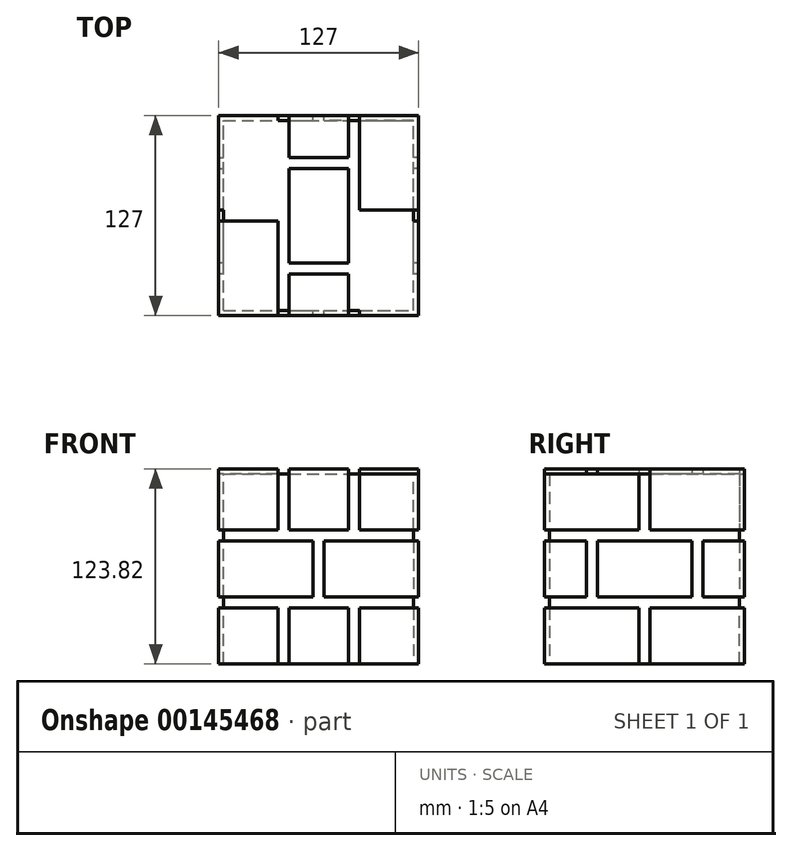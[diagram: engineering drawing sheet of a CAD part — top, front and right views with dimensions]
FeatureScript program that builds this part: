
annotation { "Feature Type Name" : "Feature", "Feature Type Description" : "" }
export const myFeature = defineFeature(function(context is Context, id is Id, definition is map)
    precondition{}
    {
        {
            var Q0;
            Q0=qCreatedBy(makeId("Front.planeOp"),FACE);
            var sketch = newSketch(context, id + "F0", { "sketchPlane" : qUnion([Q0])});
            skLineSegment(sketch, "E0.bottom", {"start": v(60.33, 60.33) * mm, "end": v(-60.33, 60.33) * mm});
            skLineSegment(sketch, "E0.top", {"start": v(60.32, -60.33) * mm, "end": v(-60.33, -60.33) * mm});
            skLineSegment(sketch, "E0.left", {"start": v(60.33, 60.33) * mm, "end": v(60.32, -60.33) * mm});
            skLineSegment(sketch, "E0.right", {"start": v(-60.33, 60.33) * mm, "end": v(-60.33, -60.33) * mm});
            skPoint(sketch, "E0.middle", {"position": v(0, 0) * mm});
            skSolve(sketch);
        }
        {
            var Q0;
            Q0 = qSketchRegion(id + "F0", true);
            extrude(context, id + "F1", {"entities" : qUnion([Q0]), "depth" : 60.32 * mm, "hasSecondDirection" : true, "secondDirectionOppositeDirection" : true, "secondDirectionDepth" : 60.32 * mm});
        }
        {
            var Q0;
            Q0=makeQuery(id+"F1.opExtrude","CAP_FACE",FACE,{"disambiguationData":[OSD([sQuery(id+"F0.wireOp",EDGE,"E0.bottom"),sQuery(id+"F0.wireOp",EDGE,"E0.top"),sQuery(id+"F0.wireOp",EDGE,"E0.left"),sQuery(id+"F0.wireOp",EDGE,"E0.right")])],"isStart":false});
            var sketch = newSketch(context, id + "F2", { "sketchPlane" : qUnion([Q0])});
            skLineSegment(sketch, "E1", {"start": v(-63.5, -60.33) * mm, "end": v(-63.5, -24.77) * mm});
            skLineSegment(sketch, "E2", {"start": v(-63.5, -24.77) * mm, "end": v(-25.9, -24.77) * mm});
            skLineSegment(sketch, "E3", {"start": v(-25.9, -24.77) * mm, "end": v(-25.9, -60.33) * mm});
            skLineSegment(sketch, "E4", {"start": v(-25.9, -60.33) * mm, "end": v(-63.5, -60.33) * mm});
            skLineSegment(sketch, "E5", {"start": v(-63.5, 17.78) * mm, "end": v(-3.5, 17.78) * mm});
            skLineSegment(sketch, "E6", {"start": v(-3.5, 17.78) * mm, "end": v(-3.5, -17.78) * mm});
            skLineSegment(sketch, "E7", {"start": v(-3.5, -17.78) * mm, "end": v(-63.5, -17.78) * mm});
            skLineSegment(sketch, "E8", {"start": v(-63.5, -17.78) * mm, "end": v(-63.5, 17.78) * mm});
            skLineSegment(sketch, "E9", {"start": v(3.5, 17.78) * mm, "end": v(3.5, -17.78) * mm});
            skLineSegment(sketch, "E10", {"start": v(3.5, -17.78) * mm, "end": v(63.5, -17.78) * mm});
            skLineSegment(sketch, "E11", {"start": v(63.5, -17.78) * mm, "end": v(63.5, 17.78) * mm});
            skLineSegment(sketch, "E12", {"start": v(63.5, 17.78) * mm, "end": v(3.5, 17.78) * mm});
            skLineSegment(sketch, "E13", {"start": v(-18.92, -60.33) * mm, "end": v(-18.92, -24.77) * mm});
            skLineSegment(sketch, "E14", {"start": v(-18.92, -24.77) * mm, "end": v(18.92, -24.77) * mm});
            skLineSegment(sketch, "E15", {"start": v(18.92, -24.77) * mm, "end": v(18.92, -60.33) * mm});
            skLineSegment(sketch, "E16", {"start": v(18.92, -60.33) * mm, "end": v(-18.92, -60.33) * mm});
            skLineSegment(sketch, "E17", {"start": v(25.9, -60.33) * mm, "end": v(25.9, -24.77) * mm});
            skLineSegment(sketch, "E18", {"start": v(25.9, -24.77) * mm, "end": v(63.5, -24.77) * mm});
            skLineSegment(sketch, "E19", {"start": v(63.5, -24.77) * mm, "end": v(63.5, -60.33) * mm});
            skLineSegment(sketch, "E20", {"start": v(63.5, -60.33) * mm, "end": v(25.9, -60.33) * mm});
            skLineSegment(sketch, "E21.MirrorCS", {"start": v(-63.5, 24.77) * mm, "end": v(-25.9, 24.77) * mm});
            skLineSegment(sketch, "E22.MirrorCS", {"start": v(-25.9, 24.77) * mm, "end": v(-25.9, 60.33) * mm});
            skLineSegment(sketch, "E23.MirrorCS", {"start": v(-25.9, 60.33) * mm, "end": v(-63.5, 60.33) * mm});
            skLineSegment(sketch, "E24.MirrorCS", {"start": v(-63.5, 60.33) * mm, "end": v(-63.5, 24.77) * mm});
            skLineSegment(sketch, "E25.MirrorCS", {"start": v(-18.92, 24.77) * mm, "end": v(18.92, 24.77) * mm});
            skLineSegment(sketch, "E26.MirrorCS", {"start": v(-18.92, 60.33) * mm, "end": v(-18.92, 24.77) * mm});
            skLineSegment(sketch, "E27.MirrorCS", {"start": v(18.92, 60.33) * mm, "end": v(-18.92, 60.33) * mm});
            skLineSegment(sketch, "E28.MirrorCS", {"start": v(18.92, 24.77) * mm, "end": v(18.92, 60.33) * mm});
            skLineSegment(sketch, "E29.MirrorCS", {"start": v(25.9, 24.77) * mm, "end": v(63.5, 24.77) * mm});
            skLineSegment(sketch, "E30.MirrorCS", {"start": v(25.9, 60.33) * mm, "end": v(25.9, 24.77) * mm});
            skLineSegment(sketch, "E31.MirrorCS", {"start": v(63.5, 60.33) * mm, "end": v(25.9, 60.33) * mm});
            skLineSegment(sketch, "E32.MirrorCS", {"start": v(63.5, 24.77) * mm, "end": v(63.5, 60.33) * mm});
            skLineSegment(sketch, "E33", {"start": v(-60.33, 24.76) * mm, "end": v(-60.33, 17.78) * mm});
            skSolve(sketch);
        }
        {
            var Q0;
            {var subQ0=sQuery(id+"F2.wireOp",EDGE,"E22.MirrorCS");Q0=makeQuery(id+"F2.imprint","IMPRINT",FACE,{"disambiguationData":[TD([[makeQuery(id+"F2.imprint","IMPRINT",EDGE,{"derivedFrom":subQ0}),1.0]])]});}
            var Q1;
            Q1=makeQuery(id+"F2.imprint","IMPRINT",FACE,{"disambiguationData":[TD([[makeQuery(id+"F2.imprint","IMPRINT",EDGE,{"derivedFrom":sQuery(id+"F2.wireOp",EDGE,"E26.MirrorCS")}),1.0]])]});
            var Q2;
            {var subQ0=sQuery(id+"F2.wireOp",EDGE,"E30.MirrorCS");Q2=makeQuery(id+"F2.imprint","IMPRINT",FACE,{"disambiguationData":[TD([[makeQuery(id+"F2.imprint","IMPRINT",EDGE,{"derivedFrom":subQ0}),1.0]])]});}
            var Q3;
            {var subQ0=sQuery(id+"F2.wireOp",EDGE,"E9");Q3=makeQuery(id+"F2.imprint","IMPRINT",FACE,{"disambiguationData":[TD([[makeQuery(id+"F2.imprint","IMPRINT",EDGE,{"derivedFrom":subQ0}),1.0]])]});}
            var Q4;
            {var subQ0=sQuery(id+"F2.wireOp",EDGE,"E6");Q4=makeQuery(id+"F2.imprint","IMPRINT",FACE,{"disambiguationData":[TD([[makeQuery(id+"F2.imprint","IMPRINT",EDGE,{"derivedFrom":subQ0}),-1.0]])]});}
            var Q5;
            {var subQ0=sQuery(id+"F2.wireOp",EDGE,"E3");Q5=makeQuery(id+"F2.imprint","IMPRINT",FACE,{"disambiguationData":[TD([[makeQuery(id+"F2.imprint","IMPRINT",EDGE,{"derivedFrom":subQ0}),-1.0]])]});}
            var Q6;
            Q6=makeQuery(id+"F2.imprint","IMPRINT",FACE,{"disambiguationData":[TD([[makeQuery(id+"F2.imprint","IMPRINT",EDGE,{"derivedFrom":sQuery(id+"F2.wireOp",EDGE,"E13")}),-1.0]])]});
            var Q7;
            {var subQ0=sQuery(id+"F2.wireOp",EDGE,"E17");Q7=makeQuery(id+"F2.imprint","IMPRINT",FACE,{"disambiguationData":[TD([[makeQuery(id+"F2.imprint","IMPRINT",EDGE,{"derivedFrom":subQ0}),-1.0]])]});}
            extrude(context, id + "F3", {"entities" : qUnion([Q0, Q1, Q2, Q3, Q4, Q5, Q6, Q7]), "operationType" : NewBodyOperationType.ADD, "depth" : 3.17 * mm});
        }
        {
            var Q0;
            {var subQ0=sQuery(id+"F0.wireOp",EDGE,"E0.left");var subQ1=makeQuery(id+"F1.opExtrude","CAP_EDGE",EDGE,{"disambiguationData":[OSD([subQ0])],"isStart":false});Q0=makeQuery(id+"F3.boolean.opBoolean","MERGE",FACE,{"derivedFrom":[makeQuery(id+"F1.opExtrude","SWEPT_FACE",FACE,{"disambiguationData":[OSD([subQ0])]}),makeQuery(id+"F3.opExtrude","SWEPT_FACE",FACE,{"disambiguationData":[OSD([subQ0]),TDD([makeQuery(id+"F2.imprint","IMPRINT",EDGE,{"disambiguationData":[TD([[makeQuery(id+"F2.imprint","INTERSECT",VERTEX,{"derivedFrom":[subQ1,sQuery(id+"F2.wireOp",EDGE,"E31.MirrorCS")]}),-1.0]])],"derivedFrom":subQ1})])]}),makeQuery(id+"F3.opExtrude","SWEPT_FACE",FACE,{"disambiguationData":[OSD([subQ0]),TDD([makeQuery(id+"F2.imprint","IMPRINT",EDGE,{"disambiguationData":[TD([[makeQuery(id+"F2.imprint","INTERSECT",VERTEX,{"derivedFrom":[subQ1,sQuery(id+"F2.wireOp",EDGE,"E20")]}),1.0]])],"derivedFrom":subQ1})])]}),makeQuery(id+"F3.opExtrude","SWEPT_FACE",FACE,{"disambiguationData":[OSD([subQ0]),TDD([makeQuery(id+"F2.imprint","IMPRINT",EDGE,{"disambiguationData":[TD([[makeQuery(id+"F2.imprint","INTERSECT",VERTEX,{"derivedFrom":[subQ1,sQuery(id+"F2.wireOp",EDGE,"E10")]}),1.0]])],"derivedFrom":subQ1})])]})]});}
            var sketch = newSketch(context, id + "F4", { "sketchPlane" : qUnion([Q0])});
            skLineSegment(sketch, "E34.bottom", {"start": v(-63.5, 17.78) * mm, "end": v(-37, 17.78) * mm});
            skLineSegment(sketch, "E34.top", {"start": v(-63.5, -17.78) * mm, "end": v(-37, -17.78) * mm});
            skLineSegment(sketch, "E34.left", {"start": v(-63.5, 17.78) * mm, "end": v(-63.5, -17.78) * mm});
            skLineSegment(sketch, "E34.right", {"start": v(-37, 17.78) * mm, "end": v(-37, -17.78) * mm});
            skLineSegment(sketch, "E35.bottom", {"start": v(-30.01, 17.78) * mm, "end": v(30, 17.78) * mm});
            skLineSegment(sketch, "E35.top", {"start": v(-30.01, -17.78) * mm, "end": v(30, -17.78) * mm});
            skLineSegment(sketch, "E35.left", {"start": v(-30.01, 17.78) * mm, "end": v(-30.01, -17.78) * mm});
            skLineSegment(sketch, "E35.right", {"start": v(30, 17.78) * mm, "end": v(30, -17.78) * mm});
            skLineSegment(sketch, "E36.bottom", {"start": v(36.98, 17.78) * mm, "end": v(63.5, 17.78) * mm});
            skLineSegment(sketch, "E36.top", {"start": v(36.98, -17.78) * mm, "end": v(63.5, -17.78) * mm});
            skLineSegment(sketch, "E36.left", {"start": v(36.98, 17.78) * mm, "end": v(36.98, -17.78) * mm});
            skLineSegment(sketch, "E36.right", {"start": v(63.5, 17.78) * mm, "end": v(63.5, -17.78) * mm});
            skLineSegment(sketch, "E37.bottom", {"start": v(-63.5, -24.76) * mm, "end": v(-3.5, -24.76) * mm});
            skLineSegment(sketch, "E37.top", {"start": v(-63.5, -60.32) * mm, "end": v(-3.5, -60.32) * mm});
            skLineSegment(sketch, "E37.left", {"start": v(-63.5, -24.76) * mm, "end": v(-63.5, -60.32) * mm});
            skLineSegment(sketch, "E37.right", {"start": v(-3.5, -24.76) * mm, "end": v(-3.5, -60.32) * mm});
            skLineSegment(sketch, "E38.bottom", {"start": v(3.5, -24.77) * mm, "end": v(63.5, -24.77) * mm});
            skLineSegment(sketch, "E38.top", {"start": v(3.5, -60.32) * mm, "end": v(63.5, -60.32) * mm});
            skLineSegment(sketch, "E38.left", {"start": v(3.5, -24.77) * mm, "end": v(3.5, -60.32) * mm});
            skLineSegment(sketch, "E38.right", {"start": v(63.5, -24.77) * mm, "end": v(63.5, -60.32) * mm});
            skLineSegment(sketch, "E39.MirrorCS", {"start": v(3.5, 24.77) * mm, "end": v(3.5, 60.33) * mm});
            skLineSegment(sketch, "E40.MirrorCS", {"start": v(3.5, 24.77) * mm, "end": v(63.5, 24.77) * mm});
            skLineSegment(sketch, "E41.MirrorCS", {"start": v(63.5, 24.77) * mm, "end": v(63.5, 60.33) * mm});
            skLineSegment(sketch, "E42.MirrorCS", {"start": v(3.5, 60.33) * mm, "end": v(63.5, 60.33) * mm});
            skLineSegment(sketch, "E43.MirrorCS", {"start": v(-3.5, 24.77) * mm, "end": v(-3.5, 60.33) * mm});
            skLineSegment(sketch, "E44.MirrorCS", {"start": v(-63.5, 24.77) * mm, "end": v(-3.5, 24.77) * mm});
            skLineSegment(sketch, "E45.MirrorCS", {"start": v(-63.5, 24.77) * mm, "end": v(-63.5, 60.33) * mm});
            skLineSegment(sketch, "E46.MirrorCS", {"start": v(-63.5, 60.33) * mm, "end": v(-3.5, 60.33) * mm});
            skSolve(sketch);
        }
        {
            var Q0;
            {var subQ1=sQuery(id+"F4.wireOp",EDGE,"E43.MirrorCS");Q0=makeQuery(id+"F4.imprint","IMPRINT",FACE,{"disambiguationData":[TD([[makeQuery(id+"F4.imprint","IMPRINT",EDGE,{"derivedFrom":subQ1}),1.0]])]});}
            var Q1;
            {var subQ0=sQuery(id+"F4.wireOp",EDGE,"E39.MirrorCS");Q1=makeQuery(id+"F4.imprint","IMPRINT",FACE,{"disambiguationData":[TD([[makeQuery(id+"F4.imprint","IMPRINT",EDGE,{"derivedFrom":subQ0}),-1.0]])]});}
            var Q2;
            {var subQ0=sQuery(id+"F4.wireOp",EDGE,"E36.left");Q2=makeQuery(id+"F4.imprint","IMPRINT",FACE,{"disambiguationData":[TD([[makeQuery(id+"F4.imprint","IMPRINT",EDGE,{"derivedFrom":subQ0}),1.0]])]});}
            var Q3;
            Q3=makeQuery(id+"F4.imprint","IMPRINT",FACE,{"disambiguationData":[TD([[makeQuery(id+"F4.imprint","IMPRINT",EDGE,{"derivedFrom":sQuery(id+"F4.wireOp",EDGE,"E35.bottom")}),-1.0]])]});
            var Q4;
            {var subQ0=sQuery(id+"F4.wireOp",EDGE,"E34.left");Q4=makeQuery(id+"F4.imprint","IMPRINT",FACE,{"disambiguationData":[TD([[makeQuery(id+"F4.imprint","IMPRINT",EDGE,{"derivedFrom":subQ0}),1.0]])]});}
            var Q5;
            Q5=makeQuery(id+"F4.imprint","IMPRINT",FACE,{"disambiguationData":[TD([[makeQuery(id+"F4.imprint","IMPRINT",EDGE,{"derivedFrom":sQuery(id+"F4.wireOp",EDGE,"E37.top")}),1.0]])]});
            var Q6;
            {var subQ0=sQuery(id+"F4.wireOp",EDGE,"E38.left");Q6=makeQuery(id+"F4.imprint","IMPRINT",FACE,{"disambiguationData":[TD([[makeQuery(id+"F4.imprint","IMPRINT",EDGE,{"derivedFrom":subQ0}),1.0]])]});}
            extrude(context, id + "F5", {"entities" : qUnion([Q0, Q1, Q2, Q3, Q4, Q5, Q6]), "operationType" : NewBodyOperationType.ADD, "depth" : 3.17 * mm});
        }
        {
            var Q0;
            {var subQ0=sQuery(id+"F0.wireOp",EDGE,"E0.left");var subQ1=makeQuery(id+"F1.opExtrude","CAP_EDGE",EDGE,{"disambiguationData":[OSD([subQ0])],"isStart":true});Q0=makeQuery(id+"F5.boolean.opBoolean","MERGE",FACE,{"derivedFrom":[makeQuery(id+"F1.opExtrude","CAP_FACE",FACE,{"disambiguationData":[OSD([sQuery(id+"F0.wireOp",EDGE,"E0.bottom"),sQuery(id+"F0.wireOp",EDGE,"E0.top"),subQ0,sQuery(id+"F0.wireOp",EDGE,"E0.right")])],"isStart":true}),makeQuery(id+"F5.opExtrude","SWEPT_FACE",FACE,{"disambiguationData":[OSD([subQ0]),TDD([makeQuery(id+"F4.imprint","IMPRINT",EDGE,{"disambiguationData":[TD([[makeQuery(id+"F4.imprint","INTERSECT",VERTEX,{"derivedFrom":[subQ1,sQuery(id+"F4.wireOp",EDGE,"E42.MirrorCS")]}),-1.0]])],"derivedFrom":subQ1})])]}),makeQuery(id+"F5.opExtrude","SWEPT_FACE",FACE,{"disambiguationData":[OSD([subQ0]),TDD([makeQuery(id+"F4.imprint","IMPRINT",EDGE,{"disambiguationData":[TD([[makeQuery(id+"F4.imprint","INTERSECT",VERTEX,{"derivedFrom":[subQ1,sQuery(id+"F4.wireOp",EDGE,"E38.top")]}),1.0]])],"derivedFrom":subQ1})])]}),makeQuery(id+"F5.opExtrude","SWEPT_FACE",FACE,{"disambiguationData":[OSD([subQ0]),TDD([makeQuery(id+"F4.imprint","IMPRINT",EDGE,{"disambiguationData":[TD([[makeQuery(id+"F4.imprint","INTERSECT",VERTEX,{"derivedFrom":[subQ1,sQuery(id+"F4.wireOp",EDGE,"E36.bottom")]}),-1.0]])],"derivedFrom":subQ1})])]})]});}
            var sketch = newSketch(context, id + "F6", { "sketchPlane" : qUnion([Q0])});
            skSolve(sketch);
        }
        {
            var Q0;
            Q0 = qSketchRegion(id + "F6", true);
            var Q1;
            Q1=makeQuery(id+"F3.opExtrude","CAP_FACE",FACE,{"disambiguationData":[OSD([sQuery(id+"F0.wireOp",EDGE,"E0.right"),sQuery(id+"F2.wireOp",EDGE,"E21.MirrorCS"),sQuery(id+"F2.wireOp",EDGE,"E22.MirrorCS"),sQuery(id+"F2.wireOp",EDGE,"E23.MirrorCS")])],"isStart":false});
            var Q2;
            Q2=makeQuery(id+"F3.opExtrude","CAP_FACE",FACE,{"disambiguationData":[OSD([sQuery(id+"F2.wireOp",EDGE,"E26.MirrorCS"),sQuery(id+"F2.wireOp",EDGE,"E27.MirrorCS"),sQuery(id+"F2.wireOp",EDGE,"E28.MirrorCS"),sQuery(id+"F2.wireOp",EDGE,"E25.MirrorCS")])],"isStart":false});
            var Q3;
            Q3=makeQuery(id+"F5.boolean.opBoolean","MERGE",FACE,{"derivedFrom":[makeQuery(id+"F3.opExtrude","CAP_FACE",FACE,{"disambiguationData":[OSD([sQuery(id+"F0.wireOp",EDGE,"E0.left"),sQuery(id+"F2.wireOp",EDGE,"E29.MirrorCS"),sQuery(id+"F2.wireOp",EDGE,"E30.MirrorCS"),sQuery(id+"F2.wireOp",EDGE,"E31.MirrorCS")])],"isStart":false}),makeQuery(id+"F5.opExtrude","SWEPT_FACE",FACE,{"disambiguationData":[OSD([sQuery(id+"F4.wireOp",EDGE,"E45.MirrorCS")])]})]});
            var Q4;
            Q4=makeQuery(id+"F5.boolean.opBoolean","MERGE",FACE,{"derivedFrom":[makeQuery(id+"F3.opExtrude","CAP_FACE",FACE,{"disambiguationData":[OSD([sQuery(id+"F0.wireOp",EDGE,"E0.left"),sQuery(id+"F2.wireOp",EDGE,"E9"),sQuery(id+"F2.wireOp",EDGE,"E10"),sQuery(id+"F2.wireOp",EDGE,"E12")])],"isStart":false}),makeQuery(id+"F5.opExtrude","SWEPT_FACE",FACE,{"disambiguationData":[OSD([sQuery(id+"F4.wireOp",EDGE,"E34.left")])]})]});
            var Q5;
            Q5=makeQuery(id+"F3.opExtrude","CAP_FACE",FACE,{"disambiguationData":[OSD([sQuery(id+"F0.wireOp",EDGE,"E0.right"),sQuery(id+"F2.wireOp",EDGE,"E5"),sQuery(id+"F2.wireOp",EDGE,"E6"),sQuery(id+"F2.wireOp",EDGE,"E7")])],"isStart":false});
            var Q6;
            Q6=makeQuery(id+"F3.opExtrude","CAP_FACE",FACE,{"disambiguationData":[OSD([sQuery(id+"F0.wireOp",EDGE,"E0.right"),sQuery(id+"F2.wireOp",EDGE,"E2"),sQuery(id+"F2.wireOp",EDGE,"E3"),sQuery(id+"F2.wireOp",EDGE,"E4")])],"isStart":false});
            var Q7;
            Q7=makeQuery(id+"F3.opExtrude","CAP_FACE",FACE,{"disambiguationData":[OSD([sQuery(id+"F2.wireOp",EDGE,"E13"),sQuery(id+"F2.wireOp",EDGE,"E14"),sQuery(id+"F2.wireOp",EDGE,"E15"),sQuery(id+"F2.wireOp",EDGE,"E16")])],"isStart":false});
            var Q8;
            Q8=makeQuery(id+"F5.boolean.opBoolean","MERGE",FACE,{"derivedFrom":[makeQuery(id+"F3.opExtrude","CAP_FACE",FACE,{"disambiguationData":[OSD([sQuery(id+"F0.wireOp",EDGE,"E0.left"),sQuery(id+"F2.wireOp",EDGE,"E17"),sQuery(id+"F2.wireOp",EDGE,"E18"),sQuery(id+"F2.wireOp",EDGE,"E20")])],"isStart":false}),makeQuery(id+"F5.opExtrude","SWEPT_FACE",FACE,{"disambiguationData":[OSD([sQuery(id+"F4.wireOp",EDGE,"E37.left")])]})]});
            extrude(context, id + "F7", {"entities" : qUnion([Q0, Q1, Q2, Q3, Q4, Q5, Q6, Q7, Q8]), "operationType" : NewBodyOperationType.ADD, "oppositeDirection" : true, "depth" : 127 * mm});
        }
        {
            var Q0;
            {var subQ0=sQuery(id+"F4.wireOp",EDGE,"E42.MirrorCS");var subQ2=sQuery(id+"F4.wireOp",EDGE,"E40.MirrorCS");var subQ4=sQuery(id+"F4.wireOp",EDGE,"E43.MirrorCS");var subQ5=sQuery(id+"F4.wireOp",EDGE,"E45.MirrorCS");var subQ8=sQuery(id+"F0.wireOp",EDGE,"E0.left");var subQ9=sQuery(id+"F4.wireOp",EDGE,"E46.MirrorCS");var subQ10=sQuery(id+"F4.wireOp",EDGE,"E44.MirrorCS");Q0=makeQuery(id+"F2uOg2WHs73iVVz_1.boolean.opBoolean","SPLIT",FACE,{"disambiguationData":[TD([makeQuery(id+"F5.opExtrude","SWEPT_FACE",FACE,{"disambiguationData":[OSD([subQ5])]})])],"derivedFrom":makeQuery(id+"F7.boolean.opBoolean","MERGE",FACE,{"derivedFrom":[makeQuery(id+"F5.opExtrude","CAP_FACE",FACE,{"disambiguationData":[OSD([subQ8,sQuery(id+"F4.wireOp",EDGE,"E39.MirrorCS"),subQ2,subQ0])],"isStart":false}),makeQuery(id+"F5.opExtrude","CAP_FACE",FACE,{"disambiguationData":[OSD([subQ4,subQ10,subQ5,subQ9])],"isStart":false}),makeQuery(id+"F7.opExtrude","SWEPT_FACE",FACE,{"disambiguationData":[OSD([subQ5])]})]})});}
            var Q1;
            {var subQ2=sQuery(id+"F4.wireOp",EDGE,"E42.MirrorCS");var subQ4=sQuery(id+"F4.wireOp",EDGE,"E40.MirrorCS");var subQ5=sQuery(id+"F4.wireOp",EDGE,"E45.MirrorCS");var subQ7=sQuery(id+"F0.wireOp",EDGE,"E0.left");var subQ8=sQuery(id+"F4.wireOp",EDGE,"E46.MirrorCS");var subQ9=sQuery(id+"F4.wireOp",EDGE,"E44.MirrorCS");var subQ10=sQuery(id+"F4.wireOp",EDGE,"E39.MirrorCS");Q1=makeQuery(id+"F2uOg2WHs73iVVz_1.boolean.opBoolean","SPLIT",FACE,{"disambiguationData":[TD([makeQuery(id+"Ff1tdaM6ffOjvrD_1.boolean.opBoolean","COPY",FACE,{"derivedFrom":makeQuery(id+"Ff1tdaM6ffOjvrD_1.opExtrude","SWEPT_FACE",FACE,{"disambiguationData":[OSD([subQ10])]})})])],"derivedFrom":makeQuery(id+"F7.boolean.opBoolean","MERGE",FACE,{"derivedFrom":[makeQuery(id+"F5.opExtrude","CAP_FACE",FACE,{"disambiguationData":[OSD([subQ7,subQ10,subQ4,subQ2])],"isStart":false}),makeQuery(id+"F5.opExtrude","CAP_FACE",FACE,{"disambiguationData":[OSD([sQuery(id+"F4.wireOp",EDGE,"E43.MirrorCS"),subQ9,subQ5,subQ8])],"isStart":false}),makeQuery(id+"F7.opExtrude","SWEPT_FACE",FACE,{"disambiguationData":[OSD([subQ5])]})]})});}
            var Q2;
            {var subQ0=sQuery(id+"F4.wireOp",EDGE,"E34.left");var subQ1=sQuery(id+"F4.wireOp",EDGE,"E34.top");var subQ3=sQuery(id+"F4.wireOp",EDGE,"E36.bottom");var subQ4=sQuery(id+"F4.wireOp",EDGE,"E36.top");var subQ5=sQuery(id+"F4.wireOp",EDGE,"E35.bottom");var subQ6=sQuery(id+"F4.wireOp",EDGE,"E35.top");var subQ8=sQuery(id+"F0.wireOp",EDGE,"E0.left");var subQ9=sQuery(id+"F4.wireOp",EDGE,"E34.bottom");var subQ10=sQuery(id+"F4.wireOp",EDGE,"E36.left");Q2=makeQuery(id+"F2uOg2WHs73iVVz_1.boolean.opBoolean","SPLIT",FACE,{"disambiguationData":[TD([makeQuery(id+"Ff1tdaM6ffOjvrD_1.boolean.opBoolean","COPY",FACE,{"derivedFrom":makeQuery(id+"Ff1tdaM6ffOjvrD_1.opExtrude","SWEPT_FACE",FACE,{"disambiguationData":[OSD([subQ10])]})})])],"derivedFrom":makeQuery(id+"F7.boolean.opBoolean","MERGE",FACE,{"derivedFrom":[makeQuery(id+"F5.opExtrude","CAP_FACE",FACE,{"disambiguationData":[OSD([subQ9,subQ1,subQ0,sQuery(id+"F4.wireOp",EDGE,"E34.right")])],"isStart":false}),makeQuery(id+"F5.opExtrude","CAP_FACE",FACE,{"disambiguationData":[OSD([subQ5,subQ6,sQuery(id+"F4.wireOp",EDGE,"E35.left"),sQuery(id+"F4.wireOp",EDGE,"E35.right")])],"isStart":false}),makeQuery(id+"F5.opExtrude","CAP_FACE",FACE,{"disambiguationData":[OSD([subQ8,subQ3,subQ4,subQ10])],"isStart":false}),makeQuery(id+"F7.opExtrude","SWEPT_FACE",FACE,{"disambiguationData":[OSD([subQ0])]})]})});}
            var Q3;
            {var subQ0=sQuery(id+"F4.wireOp",EDGE,"E34.left");var subQ1=sQuery(id+"F4.wireOp",EDGE,"E34.top");var subQ3=sQuery(id+"F4.wireOp",EDGE,"E36.bottom");var subQ4=sQuery(id+"F4.wireOp",EDGE,"E35.left");var subQ5=sQuery(id+"F4.wireOp",EDGE,"E36.top");var subQ6=sQuery(id+"F4.wireOp",EDGE,"E35.bottom");var subQ7=sQuery(id+"F4.wireOp",EDGE,"E35.top");var subQ8=sQuery(id+"F4.wireOp",EDGE,"E34.bottom");var subQ10=sQuery(id+"F4.wireOp",EDGE,"E35.right");Q3=makeQuery(id+"F2uOg2WHs73iVVz_1.boolean.opBoolean","SPLIT",FACE,{"disambiguationData":[TD([makeQuery(id+"Ff1tdaM6ffOjvrD_1.boolean.opBoolean","COPY",FACE,{"derivedFrom":makeQuery(id+"Ff1tdaM6ffOjvrD_1.opExtrude","SWEPT_FACE",FACE,{"disambiguationData":[OSD([subQ4])]})})])],"derivedFrom":makeQuery(id+"F7.boolean.opBoolean","MERGE",FACE,{"derivedFrom":[makeQuery(id+"F5.opExtrude","CAP_FACE",FACE,{"disambiguationData":[OSD([subQ8,subQ1,subQ0,sQuery(id+"F4.wireOp",EDGE,"E34.right")])],"isStart":false}),makeQuery(id+"F5.opExtrude","CAP_FACE",FACE,{"disambiguationData":[OSD([subQ6,subQ7,subQ4,subQ10])],"isStart":false}),makeQuery(id+"F5.opExtrude","CAP_FACE",FACE,{"disambiguationData":[OSD([sQuery(id+"F0.wireOp",EDGE,"E0.left"),subQ3,subQ5,sQuery(id+"F4.wireOp",EDGE,"E36.left")])],"isStart":false}),makeQuery(id+"F7.opExtrude","SWEPT_FACE",FACE,{"disambiguationData":[OSD([subQ0])]})]})});}
            var Q4;
            {var subQ0=sQuery(id+"F4.wireOp",EDGE,"E36.top");var subQ1=sQuery(id+"F4.wireOp",EDGE,"E35.bottom");var subQ2=sQuery(id+"F4.wireOp",EDGE,"E35.top");var subQ3=sQuery(id+"F4.wireOp",EDGE,"E34.top");var subQ4=sQuery(id+"F4.wireOp",EDGE,"E34.left");var subQ5=sQuery(id+"F4.wireOp",EDGE,"E36.bottom");var subQ6=sQuery(id+"F4.wireOp",EDGE,"E34.right");var subQ9=sQuery(id+"F0.wireOp",EDGE,"E0.left");var subQ10=sQuery(id+"F4.wireOp",EDGE,"E34.bottom");Q4=makeQuery(id+"F2uOg2WHs73iVVz_1.boolean.opBoolean","SPLIT",FACE,{"disambiguationData":[TD([makeQuery(id+"F5.opExtrude","SWEPT_FACE",FACE,{"disambiguationData":[OSD([subQ4])]})])],"derivedFrom":makeQuery(id+"F7.boolean.opBoolean","MERGE",FACE,{"derivedFrom":[makeQuery(id+"F5.opExtrude","CAP_FACE",FACE,{"disambiguationData":[OSD([subQ10,subQ3,subQ4,subQ6])],"isStart":false}),makeQuery(id+"F5.opExtrude","CAP_FACE",FACE,{"disambiguationData":[OSD([subQ1,subQ2,sQuery(id+"F4.wireOp",EDGE,"E35.left"),sQuery(id+"F4.wireOp",EDGE,"E35.right")])],"isStart":false}),makeQuery(id+"F5.opExtrude","CAP_FACE",FACE,{"disambiguationData":[OSD([subQ9,subQ5,subQ0,sQuery(id+"F4.wireOp",EDGE,"E36.left")])],"isStart":false}),makeQuery(id+"F7.opExtrude","SWEPT_FACE",FACE,{"disambiguationData":[OSD([subQ4])]})]})});}
            var Q5;
            {var subQ0=sQuery(id+"F4.wireOp",EDGE,"E38.bottom");var subQ2=sQuery(id+"F4.wireOp",EDGE,"E37.top");var subQ4=sQuery(id+"F4.wireOp",EDGE,"E37.bottom");var subQ7=sQuery(id+"F4.wireOp",EDGE,"E37.left");var subQ8=sQuery(id+"F0.wireOp",EDGE,"E0.left");var subQ9=sQuery(id+"F4.wireOp",EDGE,"E38.top");var subQ10=sQuery(id+"F4.wireOp",EDGE,"E37.right");Q5=makeQuery(id+"F2uOg2WHs73iVVz_1.boolean.opBoolean","SPLIT",FACE,{"disambiguationData":[TD([makeQuery(id+"F5.opExtrude","SWEPT_FACE",FACE,{"disambiguationData":[OSD([subQ7])]})])],"derivedFrom":makeQuery(id+"F7.boolean.opBoolean","MERGE",FACE,{"derivedFrom":[makeQuery(id+"F5.opExtrude","CAP_FACE",FACE,{"disambiguationData":[OSD([subQ4,subQ2,subQ7,subQ10])],"isStart":false}),makeQuery(id+"F5.opExtrude","CAP_FACE",FACE,{"disambiguationData":[OSD([subQ8,subQ0,subQ9,sQuery(id+"F4.wireOp",EDGE,"E38.left")])],"isStart":false}),makeQuery(id+"F7.opExtrude","SWEPT_FACE",FACE,{"disambiguationData":[OSD([subQ7])]})]})});}
            var Q6;
            {var subQ0=sQuery(id+"F4.wireOp",EDGE,"E38.top");var subQ2=sQuery(id+"F4.wireOp",EDGE,"E38.bottom");var subQ4=sQuery(id+"F4.wireOp",EDGE,"E37.top");var subQ6=sQuery(id+"F4.wireOp",EDGE,"E37.bottom");var subQ8=sQuery(id+"F4.wireOp",EDGE,"E37.left");var subQ9=sQuery(id+"F0.wireOp",EDGE,"E0.left");var subQ10=sQuery(id+"F4.wireOp",EDGE,"E38.left");Q6=makeQuery(id+"F2uOg2WHs73iVVz_1.boolean.opBoolean","SPLIT",FACE,{"disambiguationData":[TD([makeQuery(id+"Ff1tdaM6ffOjvrD_1.boolean.opBoolean","COPY",FACE,{"derivedFrom":makeQuery(id+"Ff1tdaM6ffOjvrD_1.opExtrude","SWEPT_FACE",FACE,{"disambiguationData":[OSD([subQ10])]})})])],"derivedFrom":makeQuery(id+"F7.boolean.opBoolean","MERGE",FACE,{"derivedFrom":[makeQuery(id+"F5.opExtrude","CAP_FACE",FACE,{"disambiguationData":[OSD([subQ6,subQ4,subQ8,sQuery(id+"F4.wireOp",EDGE,"E37.right")])],"isStart":false}),makeQuery(id+"F5.opExtrude","CAP_FACE",FACE,{"disambiguationData":[OSD([subQ9,subQ2,subQ0,subQ10])],"isStart":false}),makeQuery(id+"F7.opExtrude","SWEPT_FACE",FACE,{"disambiguationData":[OSD([subQ8])]})]})});}
            extrude(context, id + "F8", {"entities" : qUnion([Q0, Q1, Q2, Q3, Q4, Q5, Q6]), "operationType" : NewBodyOperationType.ADD, "oppositeDirection" : true, "depth" : 127 * mm});
        }
        {
            var Q0;
            {var subQ21=sQuery(id+"F2.wireOp",EDGE,"E3");Q0=makeQuery(id+"F2.imprint","IMPRINT",FACE,{"disambiguationData":[TD([[makeQuery(id+"F2.imprint","IMPRINT",EDGE,{"derivedFrom":subQ21}),1.0]])]});}
            extrude(context, id + "F9", {"entities" : qUnion([Q0]), "operationType" : NewBodyOperationType.REMOVE, "depth" : 25.4 * mm});
        }
        {
            var Q0;
            {var subQ30=sQuery(id+"F4.wireOp",EDGE,"E34.right");Q0=makeQuery(id+"F4.imprint","IMPRINT",FACE,{"disambiguationData":[TD([[makeQuery(id+"F4.imprint","IMPRINT",EDGE,{"derivedFrom":subQ30}),1.0]])]});}
            extrude(context, id + "F10", {"entities" : qUnion([Q0]), "operationType" : NewBodyOperationType.REMOVE, "depth" : 25.4 * mm});
        }
        {
            var Q0;
            {var subQ0=sQuery(id+"F4.wireOp",EDGE,"E34.left");Q0=makeQuery(id+"F8.boolean.opBoolean","MERGE",FACE,{"derivedFrom":[makeQuery(id+"F7.opExtrude","CAP_FACE",FACE,{"disambiguationData":[OSD([sQuery(id+"F0.wireOp",EDGE,"E0.right"),sQuery(id+"F2.wireOp",EDGE,"E5"),sQuery(id+"F2.wireOp",EDGE,"E6"),sQuery(id+"F2.wireOp",EDGE,"E7")])],"isStart":false}),makeQuery(id+"F7.opExtrude","CAP_FACE",FACE,{"disambiguationData":[OSD([sQuery(id+"F0.wireOp",EDGE,"E0.left"),sQuery(id+"F2.wireOp",EDGE,"E9"),sQuery(id+"F2.wireOp",EDGE,"E10"),sQuery(id+"F2.wireOp",EDGE,"E12"),subQ0])],"isStart":false}),makeQuery(id+"F8.opExtrude","SWEPT_FACE",FACE,{"disambiguationData":[OSD([subQ0]),TDD([makeQuery(id+"F7.opExtrude","CAP_EDGE",EDGE,{"disambiguationData":[OSD([subQ0])],"isStart":false})])]})]});}
            var sketch = newSketch(context, id + "F11", { "sketchPlane" : qUnion([Q0])});
            skLineSegment(sketch, "E47.bottom", {"start": v(-3.5, 17.78) * mm, "end": v(-63.5, 17.78) * mm});
            skLineSegment(sketch, "E47.top", {"start": v(-3.5, -17.78) * mm, "end": v(-63.5, -17.78) * mm});
            skLineSegment(sketch, "E47.left", {"start": v(-3.5, 17.78) * mm, "end": v(-3.5, -17.78) * mm});
            skLineSegment(sketch, "E47.right", {"start": v(-63.5, 17.78) * mm, "end": v(-63.5, -17.78) * mm});
            skLineSegment(sketch, "E48.bottom", {"start": v(63.5, -17.78) * mm, "end": v(3.5, -17.78) * mm});
            skLineSegment(sketch, "E48.top", {"start": v(63.5, 17.78) * mm, "end": v(3.5, 17.78) * mm});
            skLineSegment(sketch, "E48.left", {"start": v(63.5, -17.78) * mm, "end": v(63.5, 17.78) * mm});
            skLineSegment(sketch, "E48.right", {"start": v(3.5, -17.78) * mm, "end": v(3.5, 17.78) * mm});
            skLineSegment(sketch, "E49.bottom", {"start": v(25.9, -60.32) * mm, "end": v(18.92, -60.32) * mm});
            skLineSegment(sketch, "E49.top", {"start": v(25.9, -24.77) * mm, "end": v(18.92, -24.77) * mm});
            skLineSegment(sketch, "E49.left", {"start": v(25.9, -60.32) * mm, "end": v(25.9, -24.77) * mm});
            skLineSegment(sketch, "E49.right", {"start": v(18.92, -60.32) * mm, "end": v(18.92, -24.77) * mm});
            skLineSegment(sketch, "E50.bottom", {"start": v(25.9, 60.33) * mm, "end": v(18.93, 60.33) * mm});
            skLineSegment(sketch, "E50.top", {"start": v(25.9, 24.77) * mm, "end": v(18.93, 24.77) * mm});
            skLineSegment(sketch, "E50.left", {"start": v(25.9, 60.33) * mm, "end": v(25.9, 24.77) * mm});
            skLineSegment(sketch, "E50.right", {"start": v(18.93, 60.33) * mm, "end": v(18.93, 24.77) * mm});
            skLineSegment(sketch, "E51.bottom", {"start": v(-25.97, 60.6) * mm, "end": v(-18.92, 60.6) * mm});
            skLineSegment(sketch, "E51.top", {"start": v(-25.97, 24.1) * mm, "end": v(-18.92, 24.1) * mm});
            skLineSegment(sketch, "E51.left", {"start": v(-25.97, 60.6) * mm, "end": v(-25.97, 24.1) * mm});
            skLineSegment(sketch, "E51.right", {"start": v(-18.92, 60.6) * mm, "end": v(-18.92, 24.1) * mm});
            skLineSegment(sketch, "E52.bottom", {"start": v(-18.92, -60.33) * mm, "end": v(-25.9, -60.33) * mm});
            skLineSegment(sketch, "E52.top", {"start": v(-18.92, -24.76) * mm, "end": v(-25.9, -24.76) * mm});
            skLineSegment(sketch, "E52.left", {"start": v(-18.92, -60.33) * mm, "end": v(-18.92, -24.76) * mm});
            skLineSegment(sketch, "E52.right", {"start": v(-25.9, -60.33) * mm, "end": v(-25.9, -24.76) * mm});
            skSolve(sketch);
        }
        {
            var Q0;
            Q0=makeQuery(id+"F11.imprint","IMPRINT",FACE,{"disambiguationData":[TD([[makeQuery(id+"F11.imprint","IMPRINT",EDGE,{"derivedFrom":sQuery(id+"F11.wireOp",EDGE,"puh5UqeU-UVrh-mJbk-Yeex-wTQ6C8WgKwEd.bottom")}),1.0]])]});
            var Q1;
            Q1=makeQuery(id+"F11.imprint","IMPRINT",FACE,{"disambiguationData":[TD([[makeQuery(id+"F11.imprint","IMPRINT",EDGE,{"derivedFrom":sQuery(id+"F11.wireOp",EDGE,"E49.bottom")}),-1.0]])]});
            var Q2;
            Q2=makeQuery(id+"F11.imprint","IMPRINT",FACE,{"disambiguationData":[TD([[makeQuery(id+"F11.imprint","IMPRINT",EDGE,{"derivedFrom":sQuery(id+"F11.wireOp",EDGE,"E50.bottom")}),1.0]])]});
            var Q3;
            Q3=makeQuery(id+"F11.imprint","IMPRINT",FACE,{"disambiguationData":[TD([[makeQuery(id+"F11.imprint","IMPRINT",EDGE,{"derivedFrom":sQuery(id+"F11.wireOp",EDGE,"E51.bottom")}),-1.0]])]});
            var Q4;
            {var subQ0=sQuery(id+"F11.wireOp",EDGE,"E47.left");Q4=makeQuery(id+"F11.imprint","IMPRINT",FACE,{"disambiguationData":[TD([[makeQuery(id+"F11.imprint","IMPRINT",EDGE,{"derivedFrom":subQ0}),1.0]])]});}
            var Q5;
            Q5=makeQuery(id+"F11.imprint","IMPRINT",FACE,{"disambiguationData":[TD([[makeQuery(id+"F11.imprint","IMPRINT",EDGE,{"derivedFrom":sQuery(id+"F11.wireOp",EDGE,"E52.bottom")}),-1.0]])]});
            extrude(context, id + "F12", {"entities" : qUnion([Q0, Q1, Q2, Q3, Q4, Q5]), "operationType" : NewBodyOperationType.REMOVE, "oppositeDirection" : true, "depth" : 3.17 * mm});
        }
        {
            var Q0;
            Q0=makeQuery(id+"F8.opExtrude","CAP_FACE",FACE,{"disambiguationData":[OSD([sQuery(id+"F0.wireOp",EDGE,"E0.left"),sQuery(id+"F4.wireOp",EDGE,"E34.bottom"),sQuery(id+"F4.wireOp",EDGE,"E34.top"),sQuery(id+"F4.wireOp",EDGE,"E34.left"),sQuery(id+"F4.wireOp",EDGE,"E34.right"),sQuery(id+"F4.wireOp",EDGE,"E35.bottom"),sQuery(id+"F4.wireOp",EDGE,"E35.top"),sQuery(id+"F4.wireOp",EDGE,"E35.left"),sQuery(id+"F4.wireOp",EDGE,"E35.right"),sQuery(id+"F4.wireOp",EDGE,"E36.bottom"),sQuery(id+"F4.wireOp",EDGE,"E36.top"),sQuery(id+"F4.wireOp",EDGE,"E36.left")])],"isStart":false});
            var sketch = newSketch(context, id + "F13", { "sketchPlane" : qUnion([Q0])});
            skLineSegment(sketch, "E53.bottom", {"start": v(-3.5, 24.17) * mm, "end": v(3.5, 24.17) * mm});
            skLineSegment(sketch, "E53.top", {"start": v(-3.5, 61.45) * mm, "end": v(3.5, 61.45) * mm});
            skLineSegment(sketch, "E53.left", {"start": v(-3.5, 24.17) * mm, "end": v(-3.5, 61.45) * mm});
            skLineSegment(sketch, "E53.right", {"start": v(3.5, 24.17) * mm, "end": v(3.5, 61.45) * mm});
            skLineSegment(sketch, "E54.bottom", {"start": v(-36.82, -18.31) * mm, "end": v(-29.9, -18.31) * mm});
            skLineSegment(sketch, "E54.top", {"start": v(-36.82, 20.54) * mm, "end": v(-29.9, 20.54) * mm});
            skLineSegment(sketch, "E54.left", {"start": v(-36.82, -18.31) * mm, "end": v(-36.82, 20.54) * mm});
            skLineSegment(sketch, "E54.right", {"start": v(-29.9, -18.31) * mm, "end": v(-29.9, 20.54) * mm});
            skLineSegment(sketch, "E55.bottom", {"start": v(29.85, -18.86) * mm, "end": v(36.83, -18.86) * mm});
            skLineSegment(sketch, "E55.top", {"start": v(29.85, 19) * mm, "end": v(36.83, 19) * mm});
            skLineSegment(sketch, "E55.left", {"start": v(29.85, -18.86) * mm, "end": v(29.85, 19) * mm});
            skLineSegment(sketch, "E55.right", {"start": v(36.83, -18.86) * mm, "end": v(36.83, 19) * mm});
            skLineSegment(sketch, "E56.bottom", {"start": v(-3.49, -60.9) * mm, "end": v(3.5, -60.9) * mm});
            skLineSegment(sketch, "E56.top", {"start": v(-3.49, -23.03) * mm, "end": v(3.5, -23.03) * mm});
            skLineSegment(sketch, "E56.left", {"start": v(-3.49, -60.9) * mm, "end": v(-3.49, -23.03) * mm});
            skLineSegment(sketch, "E56.right", {"start": v(3.5, -60.9) * mm, "end": v(3.5, -23.03) * mm});
            skSolve(sketch);
        }
        {
            var Q0;
            Q0 = qSketchRegion(id + "F13", true);
            extrude(context, id + "F14", {"entities" : qUnion([Q0]), "operationType" : NewBodyOperationType.REMOVE, "oppositeDirection" : true, "depth" : 3.17 * mm});
        }
        {
            var Q0;
            {var subQ0=sQuery(id+"F4.wireOp",EDGE,"E46.MirrorCS");var subQ1=sQuery(id+"F4.wireOp",EDGE,"E45.MirrorCS");var subQ2=sQuery(id+"F4.wireOp",EDGE,"E42.MirrorCS");var subQ3=sQuery(id+"F2.wireOp",EDGE,"E31.MirrorCS");var subQ4=sQuery(id+"F2.wireOp",EDGE,"E27.MirrorCS");var subQ5=sQuery(id+"F2.wireOp",EDGE,"E23.MirrorCS");Q0=makeQuery(id+"F8.boolean.opBoolean","MERGE",FACE,{"derivedFrom":[makeQuery(id+"F7.boolean.opBoolean","MERGE",FACE,{"derivedFrom":[makeQuery(id+"F5.boolean.opBoolean","MERGE",FACE,{"derivedFrom":[makeQuery(id+"F3.boolean.opBoolean","MERGE",FACE,{"derivedFrom":[makeQuery(id+"F1.opExtrude","SWEPT_FACE",FACE,{"disambiguationData":[OSD([sQuery(id+"F0.wireOp",EDGE,"E0.bottom")])]}),makeQuery(id+"F3.opExtrude","SWEPT_FACE",FACE,{"disambiguationData":[OSD([subQ5])]}),makeQuery(id+"F3.opExtrude","SWEPT_FACE",FACE,{"disambiguationData":[OSD([subQ4])]}),makeQuery(id+"F3.opExtrude","SWEPT_FACE",FACE,{"disambiguationData":[OSD([subQ3])]})]}),makeQuery(id+"F5.opExtrude","SWEPT_FACE",FACE,{"disambiguationData":[OSD([subQ2])]}),makeQuery(id+"F5.opExtrude","SWEPT_FACE",FACE,{"disambiguationData":[OSD([subQ0])]})]}),makeQuery(id+"F7.opExtrude","SWEPT_FACE",FACE,{"disambiguationData":[OSD([subQ5])]}),makeQuery(id+"F7.opExtrude","SWEPT_FACE",FACE,{"disambiguationData":[OSD([subQ4])]}),makeQuery(id+"F7.opExtrude","SWEPT_FACE",FACE,{"disambiguationData":[OSD([subQ3,subQ1,subQ0])]})]}),makeQuery(id+"F8.opExtrude","SWEPT_FACE",FACE,{"disambiguationData":[OSD([subQ2,subQ1,subQ0])]})]});}
            var sketch = newSketch(context, id + "F15", { "sketchPlane" : qUnion([Q0])});
            skLineSegment(sketch, "E57", {"start": v(-25.9, 63.5) * mm, "end": v(-25.9, -63.5) * mm});
            skLineSegment(sketch, "E58", {"start": v(-63.5, 3.5) * mm, "end": v(63.5, 3.5) * mm});
            skLineSegment(sketch, "E59", {"start": v(-63.5, -3.5) * mm, "end": v(63.5, -3.5) * mm});
            skLineSegment(sketch, "E60", {"start": v(-18.92, -63.5) * mm, "end": v(-18.93, 63.5) * mm});
            skLineSegment(sketch, "E61", {"start": v(18.92, 63.5) * mm, "end": v(18.92, -63.5) * mm});
            skLineSegment(sketch, "E62", {"start": v(25.97, 63.5) * mm, "end": v(25.9, -63.5) * mm});
            skLineSegment(sketch, "E63", {"start": v(-18.93, 36.99) * mm, "end": v(18.92, 36.99) * mm});
            skLineSegment(sketch, "E64", {"start": v(-18.92, -36.99) * mm, "end": v(18.92, -36.99) * mm});
            skLineSegment(sketch, "E65", {"start": v(18.92, 63.5) * mm, "end": v(18.92, 36.99) * mm});
            skLineSegment(sketch, "E66", {"start": v(18.92, -36.99) * mm, "end": v(18.92, -63.5) * mm});
            skLineSegment(sketch, "E67", {"start": v(-18.92, -30) * mm, "end": v(18.92, -30) * mm});
            skLineSegment(sketch, "E68", {"start": v(-18.93, 30) * mm, "end": v(18.92, 30) * mm});
            skSolve(sketch);
        }
        {
            var Q0;
            {var subQ12=sQuery(id+"F11.wireOp",EDGE,"E50.left");var subQ30=sQuery(id+"F11.wireOp",EDGE,"E50.bottom");var subQ31=makeQuery(id+"F12.boolean.opBoolean","COPY",EDGE,{"derivedFrom":makeQuery(id+"F12.opExtrude","SWEPT_EDGE",EDGE,{"disambiguationData":[OSD([subQ30,subQ12])]})});Q0=makeQuery(id+"F15.imprint","IMPRINT",FACE,{"disambiguationData":[TD([[makeQuery(id+"F15.imprint","IMPRINT",EDGE,{"derivedFrom":subQ31}),1.0]])]});}
            var Q1;
            {var subQ1=sQuery(id+"F4.wireOp",EDGE,"E42.MirrorCS");var subQ8=sQuery(id+"F4.wireOp",EDGE,"E45.MirrorCS");var subQ9=makeQuery(id+"F5.opExtrude","SWEPT_FACE",FACE,{"disambiguationData":[OSD([subQ8])]});var subQ14=sQuery(id+"F4.wireOp",EDGE,"E46.MirrorCS");var subQ30=makeQuery(id+"F14.boolean.opBoolean","SPLIT",EDGE,{"disambiguationData":[TD([subQ9])],"derivedFrom":makeQuery(id+"F8.opExtrude","CAP_EDGE",EDGE,{"disambiguationData":[OSD([subQ1,subQ8,subQ14])],"isStart":false})});Q1=makeQuery(id+"F15.imprint","IMPRINT",FACE,{"disambiguationData":[TD([[makeQuery(id+"F15.imprint","IMPRINT",EDGE,{"derivedFrom":subQ30}),-1.0]])]});}
            var Q2;
            {var subQ4=sQuery(id+"F15.wireOp",EDGE,"E64");Q2=makeQuery(id+"F15.imprint","IMPRINT",FACE,{"disambiguationData":[TD([[makeQuery(id+"F15.imprint","IMPRINT",EDGE,{"derivedFrom":subQ4}),-1.0]])]});}
            var Q3;
            {var subQ5=sQuery(id+"F15.wireOp",EDGE,"E67");Q3=makeQuery(id+"F15.imprint","IMPRINT",FACE,{"disambiguationData":[TD([[makeQuery(id+"F15.imprint","IMPRINT",EDGE,{"derivedFrom":subQ5}),1.0]])]});}
            var Q4;
            {var subQ0=sQuery(id+"F15.wireOp",EDGE,"E60");var subQ1=sQuery(id+"F15.wireOp",EDGE,"E58");var subQ2=makeQuery(id+"F15.imprint","INTERSECT",VERTEX,{"derivedFrom":[subQ1,subQ0]});Q4=makeQuery(id+"F15.imprint","IMPRINT",FACE,{"disambiguationData":[TD([[makeQuery(id+"F15.imprint","IMPRINT",EDGE,{"disambiguationData":[TD([[subQ2,-1.0]])],"derivedFrom":subQ1}),-1.0]])]});}
            var Q5;
            {var subQ5=sQuery(id+"F15.wireOp",EDGE,"E68");Q5=makeQuery(id+"F15.imprint","IMPRINT",FACE,{"disambiguationData":[TD([[makeQuery(id+"F15.imprint","IMPRINT",EDGE,{"derivedFrom":subQ5}),-1.0]])]});}
            var Q6;
            {var subQ1=sQuery(id+"F15.wireOp",EDGE,"E63");Q6=makeQuery(id+"F15.imprint","IMPRINT",FACE,{"disambiguationData":[TD([[makeQuery(id+"F15.imprint","IMPRINT",EDGE,{"derivedFrom":subQ1}),1.0]])]});}
            var Q7;
            {var subQ0=sQuery(id+"F11.wireOp",EDGE,"E51.left");var subQ1=makeQuery(id+"F12.opExtrude","SWEPT_FACE",FACE,{"disambiguationData":[OSD([subQ0])]});var subQ2=sQuery(id+"F4.wireOp",EDGE,"E46.MirrorCS");var subQ3=sQuery(id+"F4.wireOp",EDGE,"E45.MirrorCS");var subQ4=sQuery(id+"F4.wireOp",EDGE,"E42.MirrorCS");var subQ5=makeQuery(id+"F8.opExtrude","SWEPT_FACE",FACE,{"disambiguationData":[OSD([subQ4,subQ3,subQ2])]});var subQ6=sQuery(id+"F2.wireOp",EDGE,"E31.MirrorCS");var subQ7=makeQuery(id+"F7.opExtrude","SWEPT_FACE",FACE,{"disambiguationData":[OSD([subQ6,subQ3,subQ2])]});var subQ8=sQuery(id+"F2.wireOp",EDGE,"E27.MirrorCS");var subQ9=makeQuery(id+"F7.opExtrude","SWEPT_FACE",FACE,{"disambiguationData":[OSD([subQ8])]});var subQ10=sQuery(id+"F2.wireOp",EDGE,"E23.MirrorCS");var subQ11=makeQuery(id+"F7.opExtrude","SWEPT_FACE",FACE,{"disambiguationData":[OSD([subQ10])]});var subQ12=makeQuery(id+"F5.opExtrude","SWEPT_FACE",FACE,{"disambiguationData":[OSD([subQ2])]});var subQ13=makeQuery(id+"F5.opExtrude","SWEPT_FACE",FACE,{"disambiguationData":[OSD([subQ4])]});var subQ14=makeQuery(id+"F3.opExtrude","SWEPT_FACE",FACE,{"disambiguationData":[OSD([subQ6])]});var subQ15=makeQuery(id+"F3.opExtrude","SWEPT_FACE",FACE,{"disambiguationData":[OSD([subQ8])]});var subQ16=makeQuery(id+"F3.opExtrude","SWEPT_FACE",FACE,{"disambiguationData":[OSD([subQ10])]});var subQ17=sQuery(id+"F0.wireOp",EDGE,"E0.bottom");var subQ18=makeQuery(id+"F1.opExtrude","SWEPT_FACE",FACE,{"disambiguationData":[OSD([subQ17])]});var subQ19=makeQuery(id+"F8.boolean.opBoolean","MERGE",FACE,{"derivedFrom":[makeQuery(id+"F7.boolean.opBoolean","MERGE",FACE,{"derivedFrom":[makeQuery(id+"F5.boolean.opBoolean","MERGE",FACE,{"derivedFrom":[makeQuery(id+"F3.boolean.opBoolean","MERGE",FACE,{"derivedFrom":[subQ18,subQ16,subQ15,subQ14]}),subQ13,subQ12]}),subQ11,subQ9,subQ7]}),subQ5]});var subQ20=makeQuery(id+"F12.boolean.opBoolean","INTERSECT",EDGE,{"derivedFrom":[subQ19,subQ1]});Q7=makeQuery(id+"F15.imprint","IMPRINT",FACE,{"disambiguationData":[TD([[makeQuery(id+"F15.imprint","IMPRINT",EDGE,{"derivedFrom":subQ20}),1.0]])]});}
            var Q8;
            {var subQ0=sQuery(id+"F4.wireOp",EDGE,"E46.MirrorCS");var subQ1=sQuery(id+"F4.wireOp",EDGE,"E43.MirrorCS");var subQ2=sQuery(id+"F2.wireOp",EDGE,"E31.MirrorCS");var subQ3=sQuery(id+"F0.wireOp",EDGE,"E0.left");var subQ4=sQuery(id+"F0.wireOp",EDGE,"E0.bottom");var subQ5=makeQuery(id+"F10.boolean.opBoolean","COPY",EDGE,{"derivedFrom":makeQuery(id+"F10.opExtrude","SWEPT_EDGE",EDGE,{"disambiguationData":[OSD([subQ4,subQ3,subQ2,subQ1,subQ0])]})});Q8=makeQuery(id+"F15.imprint","IMPRINT",FACE,{"disambiguationData":[TD([[makeQuery(id+"F15.imprint","IMPRINT",EDGE,{"derivedFrom":subQ5}),1.0]])]});}
            extrude(context, id + "F16", {"entities" : qUnion([Q0, Q1, Q2, Q3, Q4, Q5, Q6, Q7, Q8]), "operationType" : NewBodyOperationType.ADD, "depth" : 3.17 * mm});
        }
    });
